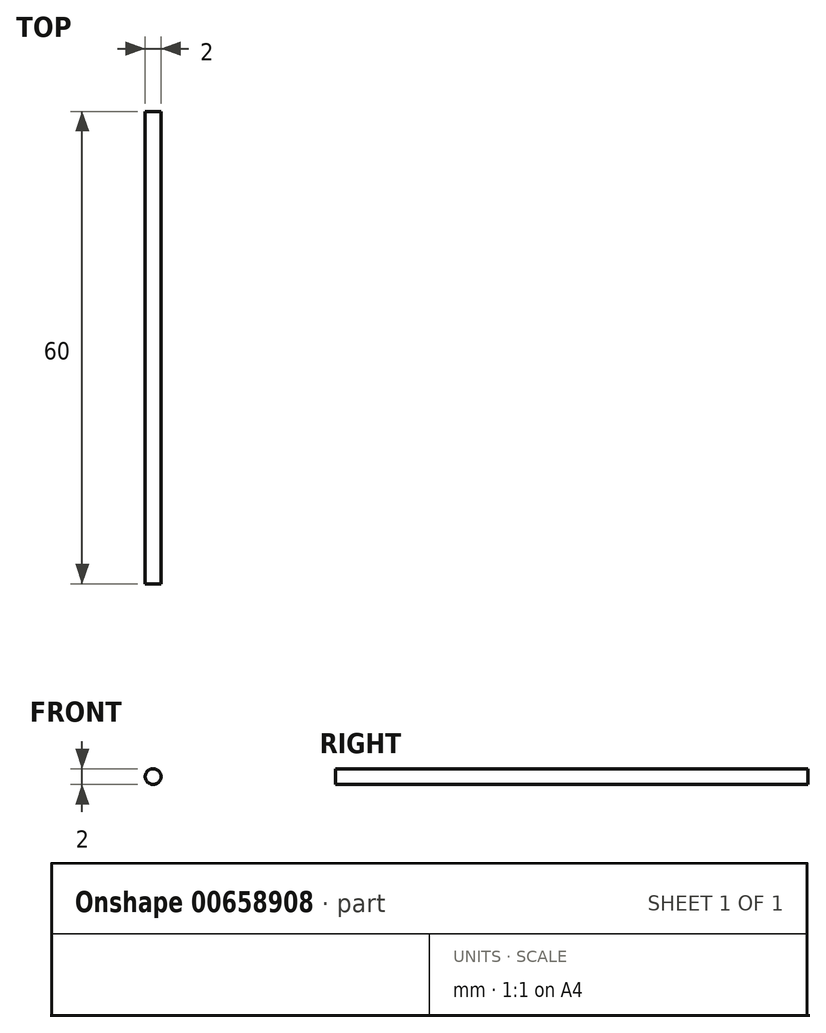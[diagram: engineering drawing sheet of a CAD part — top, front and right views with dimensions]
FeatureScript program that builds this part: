
annotation { "Feature Type Name" : "Feature", "Feature Type Description" : "" }
export const myFeature = defineFeature(function(context is Context, id is Id, definition is map)
    precondition{}
    {
        {
            var Q0;
            Q0=qCreatedBy(makeId("Front.planeOp"),FACE);
            var sketch = newSketch(context, id + "F0", { "sketchPlane" : qUnion([Q0])});
            skCircle(sketch, "E0", {"center": v(0, 0) * mm, "radius": 1 * mm});
            skSolve(sketch);
        }
        {
            var Q0;
            Q0=makeQuery(id+"F0.imprint","IMPRINT",FACE,{"disambiguationData":[TD([[makeQuery(id+"F0.imprint","IMPRINT",EDGE,{"derivedFrom":sQuery(id+"F0.wireOp",EDGE,"E0")}),1.0]])]});
            extrude(context, id + "F1", {"entities" : qUnion([Q0]), "depth" : 60 * mm, "offsetDistance" : 25.4 * mm});
        }
    });
